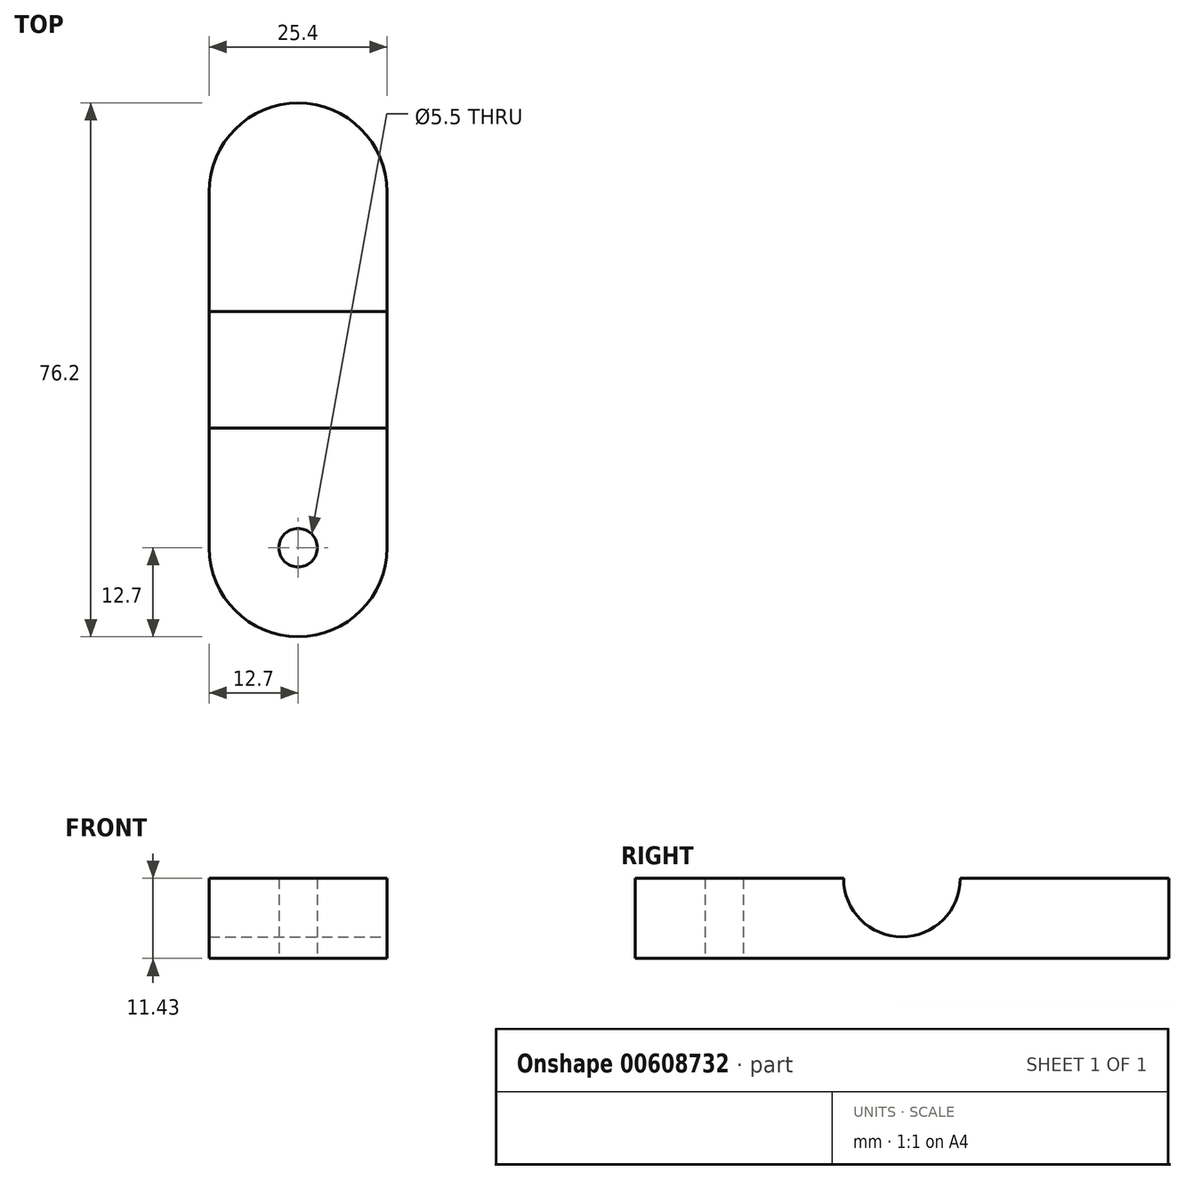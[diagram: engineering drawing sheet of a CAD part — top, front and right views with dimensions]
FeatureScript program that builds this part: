
annotation { "Feature Type Name" : "Feature", "Feature Type Description" : "" }
export const myFeature = defineFeature(function(context is Context, id is Id, definition is map)
    precondition{}
    {
        {
            var Q0;
            Q0=qCreatedBy(makeId("Top.planeOp"),FACE);
            var sketch = newSketch(context, id + "F0", { "sketchPlane" : qUnion([Q0])});
            skLineSegment(sketch, "E0.bottom", {"start": v(12.7, -38.1) * mm, "end": v(-12.7, -38.1) * mm});
            skLineSegment(sketch, "E0.top", {"start": v(12.7, 38.1) * mm, "end": v(-12.7, 38.1) * mm});
            skLineSegment(sketch, "E0.left", {"start": v(12.7, -38.1) * mm, "end": v(12.7, 38.1) * mm});
            skLineSegment(sketch, "E0.right", {"start": v(-12.7, -38.1) * mm, "end": v(-12.7, 38.1) * mm});
            skPoint(sketch, "E0.middle", {"position": v(0, 0) * mm});
            skSolve(sketch);
        }
        {
            var Q0;
            Q0=makeQuery(id+"F0.imprint","IMPRINT",FACE,{"disambiguationData":[TD([[makeQuery(id+"F0.imprint","IMPRINT",EDGE,{"derivedFrom":sQuery(id+"F0.wireOp",EDGE,"E0.bottom")}),-1.0]])]});
            extrude(context, id + "F1", {"entities" : qUnion([Q0]), "depth" : 11.43 * mm, "offsetDistance" : 25.4 * mm});
        }
        {
            var Q0;
            Q0=qCreatedBy(makeId("Right.planeOp"),FACE);
            var sketch = newSketch(context, id + "F2", { "sketchPlane" : qUnion([Q0])});
            skLineSegment(sketch, "E1.0", {"start": v(-38.1, 11.43) * mm, "end": v(38.1, 11.43) * mm, "construction": true});
            skArc(sketch, "E2", {"start": v(-8.33, 11.43) * mm, "mid": v(0, 3.1) * mm, "end": v(8.33, 11.43) * mm});
            skLineSegment(sketch, "E3", {"start": v(8.33, 11.43) * mm, "end": v(-8.33, 11.43) * mm});
            skSolve(sketch);
        }
        {
            var Q0;
            Q0 = qSketchRegion(id + "F2", true);
            extrude(context, id + "F3", {"entities" : qUnion([Q0]), "operationType" : NewBodyOperationType.REMOVE, "endBound" : BoundingType.THROUGH_ALL, "oppositeDirection" : true, "depth" : 25.4 * mm, "offsetDistance" : 25.4 * mm, "hasSecondDirection" : true, "secondDirectionBound" : SecondDirectionBoundingType.THROUGH_ALL, "secondDirectionOppositeDirection" : false, "secondDirectionDepth" : 25.4 * mm});
        }
        {
            var Q0;
            Q0=qCreatedBy(makeId("Top.planeOp"),FACE);
            var sketch = newSketch(context, id + "F4", { "sketchPlane" : qUnion([Q0])});
            skPoint(sketch, "E4", {"position": v(0, -25.4) * mm});
            skPoint(sketch, "E5", {"position": v(0, -12.7) * mm});
            skSolve(sketch);
        }
        {
            var Q0;
            Q0=sQuery(id+"F4.wireOp",VERTEX,"E4");
            var Q1;
            Q1=makeQuery(id+"F1.opExtrude","SWEPT_BODY",BODY,{"disambiguationData":[OSD([sQuery(id+"F0.wireOp",EDGE,"E0.bottom"),sQuery(id+"F0.wireOp",EDGE,"E0.top"),sQuery(id+"F0.wireOp",EDGE,"E0.left"),sQuery(id+"F0.wireOp",EDGE,"E0.right")])]});
            hole(context, id + "F5", {"style" : HoleStyle.SIMPLE, "endStyle" : HoleEndStyle.THROUGH, "oppositeDirection" : true, "standardTappedOrClearance" : lookupTablePath({ "standard" : "ISO", "fit" : "Normal", "size" : "M5", "type" : "Clearance" }), "standardBlindInLast" : lookupTablePath({ "fit" : "Standard", "standard" : "ISO", "size" : "M5", "type" : "Clearance" }), "holeDiameter" : 5.5 * mm, "majorDiameter" : 6.35 * mm, "isTappedThrough" : true, "tappedDepth" : 12.7 * mm, "tapClearance" : 3, "locations" : qUnion([Q0]), "scope" : qUnion([Q1])});
        }
        {
            var Q0;
            Q0=makeQuery(id+"F1.opExtrude","SWEPT_EDGE",EDGE,{"disambiguationData":[OSD([sQuery(id+"F0.wireOp",EDGE,"E0.bottom"),sQuery(id+"F0.wireOp",EDGE,"E0.right")])]});
            var Q1;
            Q1=makeQuery(id+"F1.opExtrude","SWEPT_EDGE",EDGE,{"disambiguationData":[OSD([sQuery(id+"F0.wireOp",EDGE,"E0.bottom"),sQuery(id+"F0.wireOp",EDGE,"E0.left")])]});
            var Q2;
            Q2=makeQuery(id+"F1.opExtrude","SWEPT_EDGE",EDGE,{"disambiguationData":[OSD([sQuery(id+"F0.wireOp",EDGE,"E0.top"),sQuery(id+"F0.wireOp",EDGE,"E0.right")])]});
            var Q3;
            Q3=makeQuery(id+"F1.opExtrude","SWEPT_EDGE",EDGE,{"disambiguationData":[OSD([sQuery(id+"F0.wireOp",EDGE,"E0.top"),sQuery(id+"F0.wireOp",EDGE,"E0.left")])]});
            fillet(context, id + "F6", {"entities" : qUnion([Q0, Q1, Q2, Q3]), "radius" : 12.7 * mm, "tangentPropagation" : true, "allowEdgeOverflow" : false});
        }
    });
